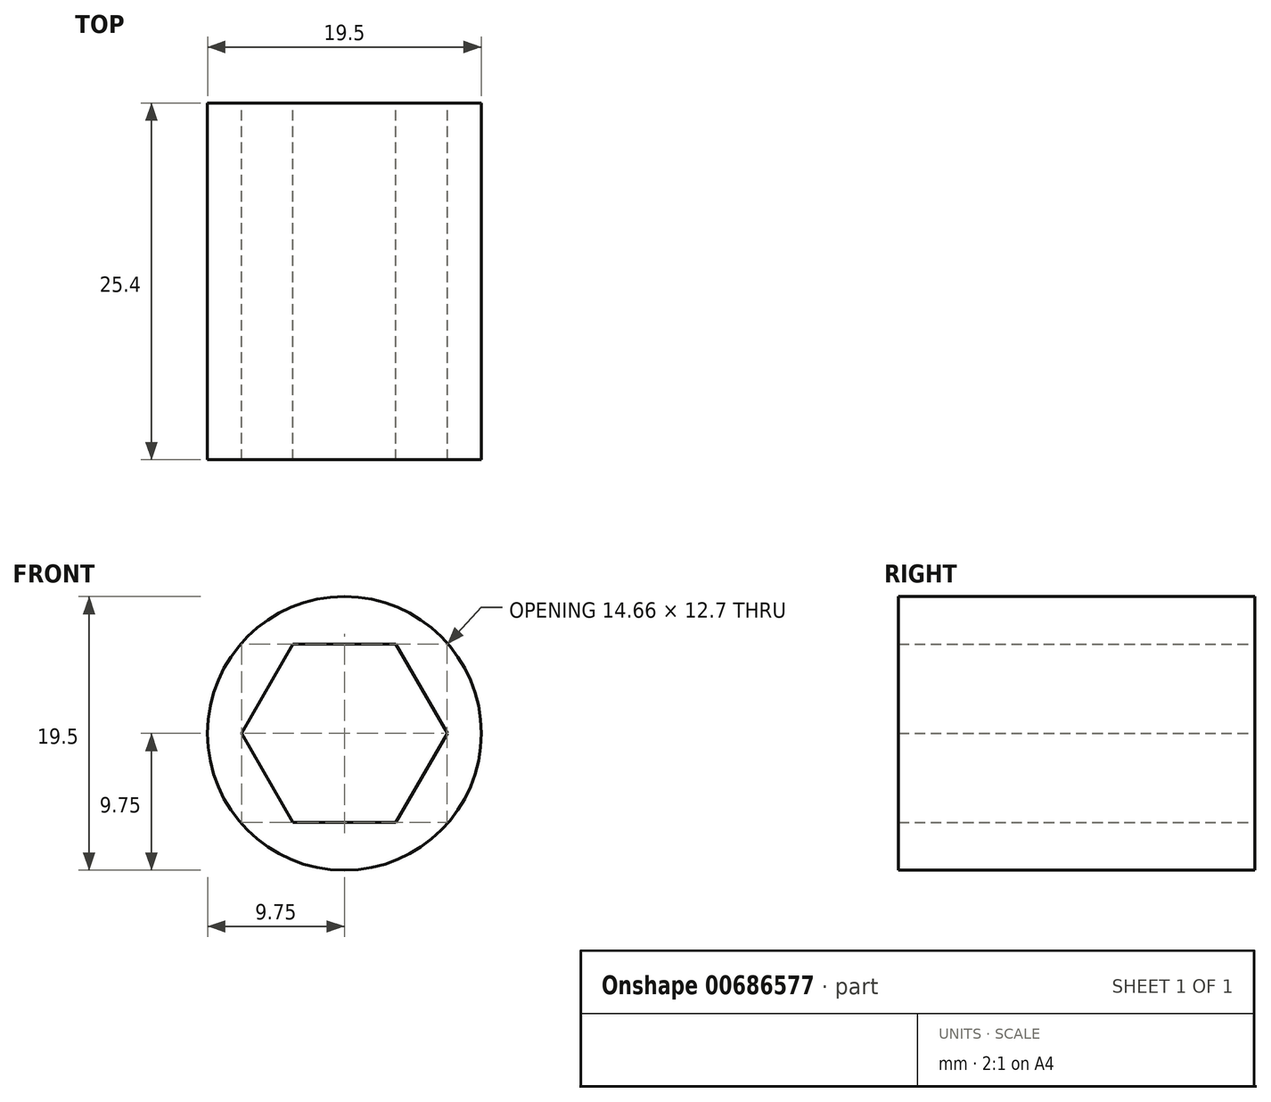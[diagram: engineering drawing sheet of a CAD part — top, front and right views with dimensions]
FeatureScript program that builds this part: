
annotation { "Feature Type Name" : "Feature", "Feature Type Description" : "" }
export const myFeature = defineFeature(function(context is Context, id is Id, definition is map)
    precondition{}
    {
        {
            var Q0;
            Q0=qCreatedBy(makeId("Front.planeOp"),FACE);
            var sketch = newSketch(context, id + "F0", { "sketchPlane" : qUnion([Q0])});
            skCircle(sketch, "E0", {"center": v(0, 0) * mm, "radius": 9.75 * mm});
            skCircle(sketch, "E1.cCircle", {"center": v(0, 0) * mm, "radius": 6.35 * mm, "construction": true});
            skLineSegment(sketch, "E1.0", {"start": v(-3.67, 6.35) * mm, "end": v(3.67, 6.35) * mm});
            skLineSegment(sketch, "E1.1", {"start": v(3.67, 6.35) * mm, "end": v(7.33, 0) * mm});
            skLineSegment(sketch, "E1.2", {"start": v(7.33, 0) * mm, "end": v(3.67, -6.35) * mm});
            skLineSegment(sketch, "E1.3", {"start": v(3.67, -6.35) * mm, "end": v(-3.67, -6.35) * mm});
            skLineSegment(sketch, "E1.4", {"start": v(-3.67, -6.35) * mm, "end": v(-7.33, 0) * mm});
            skLineSegment(sketch, "E1.5", {"start": v(-7.33, 0) * mm, "end": v(-3.67, 6.35) * mm});
            skPoint(sketch, "E1.0.midPoint", {"position": v(0, 6.35) * mm});
            skSolve(sketch);
        }
        {
            var Q0;
            Q0=makeQuery(id+"F0.imprint","IMPRINT",FACE,{"disambiguationData":[TD([[makeQuery(id+"F0.imprint","IMPRINT",EDGE,{"derivedFrom":sQuery(id+"F0.wireOp",EDGE,"E0")}),1.0]])]});
            extrude(context, id + "F1", {"entities" : qUnion([Q0]), "endBound" : BoundingType.SYMMETRIC, "depth" : 25.4 * mm, "offsetDistance" : 25.4 * mm});
        }
    });
